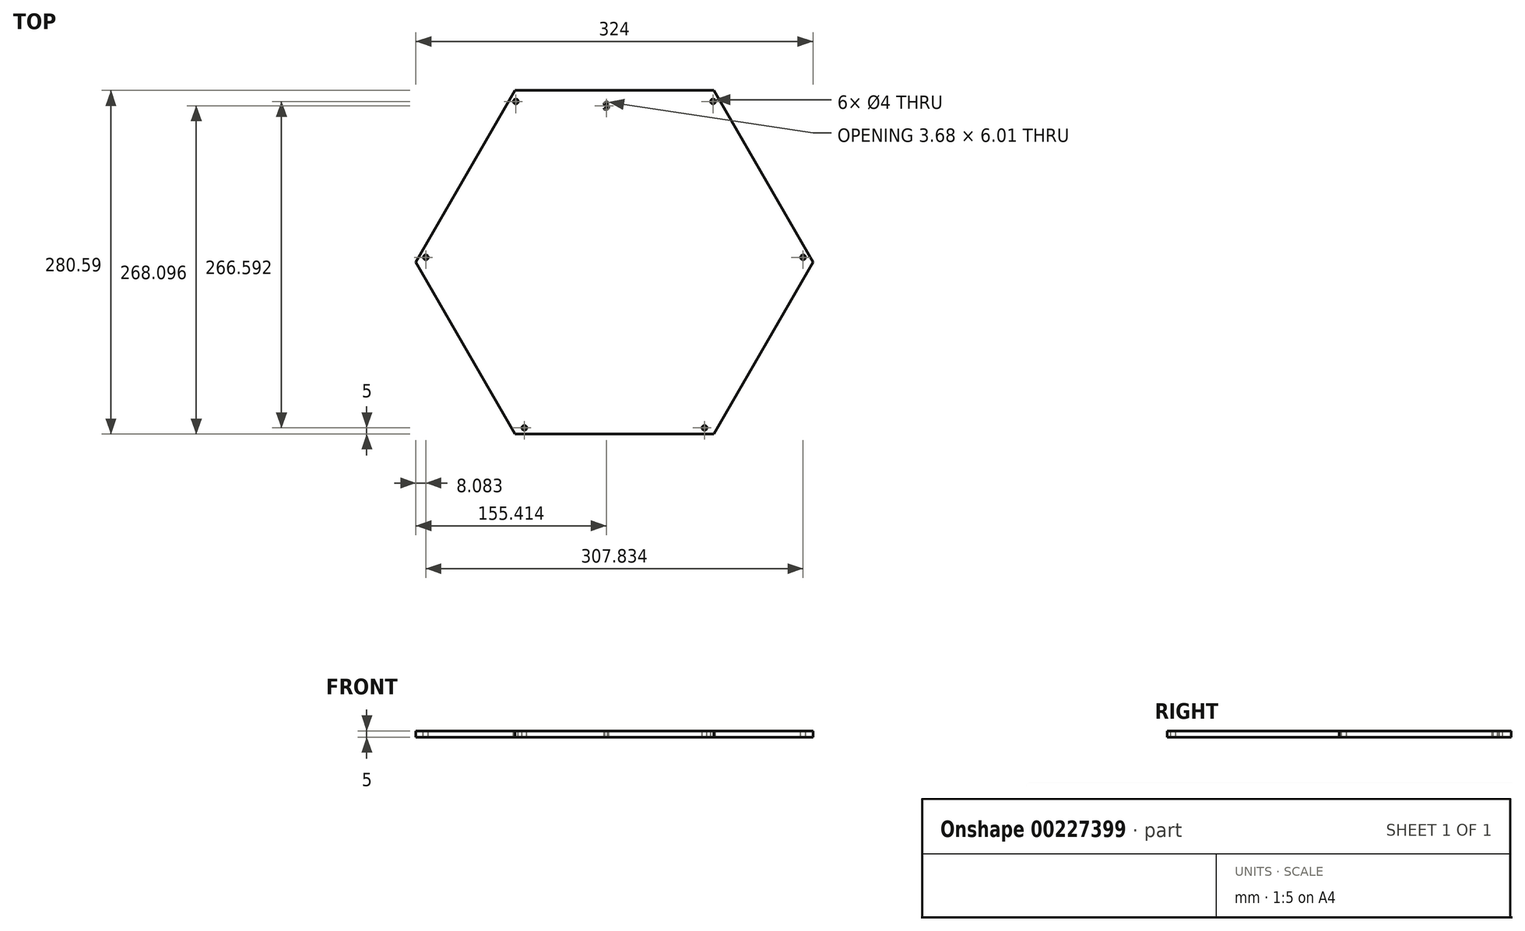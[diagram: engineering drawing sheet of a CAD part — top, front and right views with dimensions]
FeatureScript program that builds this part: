
annotation { "Feature Type Name" : "Feature", "Feature Type Description" : "" }
export const myFeature = defineFeature(function(context is Context, id is Id, definition is map)
    precondition{}
    {
        {
            var Q0;
            Q0=qCreatedBy(makeId("Top.planeOp"),FACE);
            var sketch = newSketch(context, id + "F0", { "sketchPlane" : qUnion([Q0])});
            skLineSegment(sketch, "E0", {"start": v(-81, 0) * mm, "end": v(81, 0) * mm});
            skLineSegment(sketch, "E1", {"start": v(-81, 280.6) * mm, "end": v(-162, 140.3) * mm});
            skCircle(sketch, "E2", {"center": v(0, 140.3) * mm, "radius": 140.3 * mm, "construction": true});
            skLineSegment(sketch, "E3.0", {"start": v(-81, 280.6) * mm, "end": v(81, 280.6) * mm});
            skLineSegment(sketch, "E3.2", {"start": v(162, 140.3) * mm, "end": v(81, 0) * mm});
            skLineSegment(sketch, "E3.4", {"start": v(-81, 0) * mm, "end": v(-162, 140.3) * mm});
            skPoint(sketch, "E3.0.midPoint", {"position": v(0, 280.6) * mm});
            skPoint(sketch, "E4.orphan", {"position": v(0, 420.89) * mm});
            skPoint(sketch, "E5.orphan", {"position": v(-243, 0) * mm});
            skPoint(sketch, "E6.orphan", {"position": v(243, 0) * mm});
            skLineSegment(sketch, "E7", {"start": v(81, 280.6) * mm, "end": v(162, 140.3) * mm});
            skSolve(sketch);
        }
        {
            var Q0;
            Q0 = qSketchRegion(id + "F0", true);
            extrude(context, id + "F1", {"entities" : qUnion([Q0]), "depth" : 5 * mm});
        }
        {
            var Q0;
            Q0=makeQuery(id+"F1.opExtrude","CAP_FACE",FACE,{"disambiguationData":[OSD([sQuery(id+"F0.wireOp",EDGE,"E0"),sQuery(id+"F0.wireOp",EDGE,"E1"),sQuery(id+"F0.wireOp",EDGE,"E3.0"),sQuery(id+"F0.wireOp",EDGE,"E3.2"),sQuery(id+"F0.wireOp",EDGE,"E3.4"),sQuery(id+"F0.wireOp",EDGE,"E7")])],"isStart":false});
            var sketch = newSketch(context, id + "F2", { "sketchPlane" : qUnion([Q0])});
            skLineSegment(sketch, "E8.0", {"start": v(-81, 271.6) * mm, "end": v(81, 271.6) * mm});
            skLineSegment(sketch, "E9.0", {"start": v(-76.67, 278.1) * mm, "end": v(-157.67, 137.8) * mm});
            skPoint(sketch, "E10", {"position": v(-80.42, 271.6) * mm});
            skPoint(sketch, "E11.centerSnap0", {"position": v(0, 271.6) * mm});
            skCircle(sketch, "E12", {"center": v(-80.42, 271.6) * mm, "radius": 2 * mm});
            skLineSegment(sketch, "E13.0", {"start": v(-73.2, 4.5) * mm, "end": v(-154.2, 144.8) * mm});
            skLineSegment(sketch, "E14.0", {"start": v(154.2, 144.8) * mm, "end": v(73.2, 4.5) * mm});
            skLineSegment(sketch, "E15.0", {"start": v(76.67, 278.1) * mm, "end": v(157.67, 137.8) * mm});
            skPoint(sketch, "E16", {"position": v(80.42, 271.6) * mm});
            skCircle(sketch, "E17", {"center": v(80.42, 271.6) * mm, "radius": 2 * mm});
            skLineSegment(sketch, "E18.0", {"start": v(-81, 5) * mm, "end": v(81, 5) * mm});
            skPoint(sketch, "E19", {"position": v(-73.5, 5) * mm});
            skPoint(sketch, "E20", {"position": v(73.5, 5) * mm});
            skPoint(sketch, "E21", {"position": v(153.92, 144.3) * mm});
            skPoint(sketch, "E22", {"position": v(-153.92, 144.3) * mm});
            skCircle(sketch, "E23", {"center": v(-153.92, 144.3) * mm, "radius": 2 * mm});
            skCircle(sketch, "E24", {"center": v(-73.5, 5) * mm, "radius": 2 * mm});
            skCircle(sketch, "E25", {"center": v(73.5, 5) * mm, "radius": 2 * mm});
            skCircle(sketch, "E26", {"center": v(153.92, 144.3) * mm, "radius": 2 * mm});
            skSolve(sketch);
        }
        {
            var Q0;
            {var subQ0=sQuery(id+"F2.wireOp",EDGE,"E9.0");var subQ1=sQuery(id+"F2.wireOp",EDGE,"E8.0");var subQ2=makeQuery(id+"F2.imprint","INTERSECT",VERTEX,{"derivedFrom":[subQ1,subQ0]});Q0=makeQuery(id+"F2.imprint","IMPRINT",FACE,{"disambiguationData":[TD([[makeQuery(id+"F2.imprint","IMPRINT",EDGE,{"disambiguationData":[TD([[subQ2,-1.0]])],"derivedFrom":subQ1}),-1.0]])]});}
            var Q1;
            {var subQ0=sQuery(id+"F2.wireOp",EDGE,"E9.0");var subQ1=sQuery(id+"F2.wireOp",EDGE,"E8.0");var subQ2=makeQuery(id+"F2.imprint","INTERSECT",VERTEX,{"derivedFrom":[subQ1,subQ0]});Q1=makeQuery(id+"F2.imprint","IMPRINT",FACE,{"disambiguationData":[TD([[makeQuery(id+"F2.imprint","IMPRINT",EDGE,{"disambiguationData":[TD([[subQ2,-1.0]])],"derivedFrom":subQ1}),1.0]])]});}
            var Q2;
            {var subQ0=sQuery(id+"F2.wireOp",EDGE,"E9.0");var subQ1=makeQuery(id+"F2.imprint","INTERSECT",VERTEX,{"derivedFrom":[sQuery(id+"F2.wireOp",EDGE,"E8.0"),subQ0]});Q2=makeQuery(id+"F2.imprint","IMPRINT",FACE,{"disambiguationData":[TD([[makeQuery(id+"F2.imprint","IMPRINT",EDGE,{"disambiguationData":[TD([[subQ1,1.0]])],"derivedFrom":subQ0}),-1.0]])]});}
            var Q3;
            {var subQ0=sQuery(id+"F2.wireOp",EDGE,"E15.0");var subQ1=makeQuery(id+"F2.imprint","INTERSECT",VERTEX,{"derivedFrom":[sQuery(id+"F2.wireOp",EDGE,"E8.0"),subQ0]});Q3=makeQuery(id+"F2.imprint","IMPRINT",FACE,{"disambiguationData":[TD([[makeQuery(id+"F2.imprint","IMPRINT",EDGE,{"disambiguationData":[TD([[subQ1,1.0]])],"derivedFrom":subQ0}),1.0]])]});}
            var Q4;
            {var subQ0=sQuery(id+"F2.wireOp",EDGE,"E15.0");var subQ1=sQuery(id+"F2.wireOp",EDGE,"E8.0");var subQ2=makeQuery(id+"F2.imprint","INTERSECT",VERTEX,{"derivedFrom":[subQ1,subQ0]});Q4=makeQuery(id+"F2.imprint","IMPRINT",FACE,{"disambiguationData":[TD([[makeQuery(id+"F2.imprint","IMPRINT",EDGE,{"disambiguationData":[TD([[subQ2,1.0]])],"derivedFrom":subQ1}),1.0]])]});}
            var Q5;
            {var subQ0=sQuery(id+"F2.wireOp",EDGE,"E15.0");var subQ1=sQuery(id+"F2.wireOp",EDGE,"E8.0");var subQ2=makeQuery(id+"F2.imprint","INTERSECT",VERTEX,{"derivedFrom":[subQ1,subQ0]});Q5=makeQuery(id+"F2.imprint","IMPRINT",FACE,{"disambiguationData":[TD([[makeQuery(id+"F2.imprint","IMPRINT",EDGE,{"disambiguationData":[TD([[subQ2,1.0]])],"derivedFrom":subQ1}),-1.0]])]});}
            var Q6;
            {var subQ0=sQuery(id+"F2.wireOp",EDGE,"E15.0");var subQ1=makeQuery(id+"F2.imprint","INTERSECT",VERTEX,{"derivedFrom":[sQuery(id+"F2.wireOp",EDGE,"E14.0"),subQ0]});Q6=makeQuery(id+"F2.imprint","IMPRINT",FACE,{"disambiguationData":[TD([[makeQuery(id+"F2.imprint","IMPRINT",EDGE,{"disambiguationData":[TD([[subQ1,1.0]])],"derivedFrom":subQ0}),1.0]])]});}
            var Q7;
            {var subQ0=sQuery(id+"F2.wireOp",EDGE,"E15.0");var subQ1=sQuery(id+"F2.wireOp",EDGE,"E14.0");var subQ2=makeQuery(id+"F2.imprint","INTERSECT",VERTEX,{"derivedFrom":[subQ1,subQ0]});Q7=makeQuery(id+"F2.imprint","IMPRINT",FACE,{"disambiguationData":[TD([[makeQuery(id+"F2.imprint","IMPRINT",EDGE,{"disambiguationData":[TD([[subQ2,-1.0]])],"derivedFrom":subQ1}),1.0]])]});}
            var Q8;
            {var subQ0=sQuery(id+"F2.wireOp",EDGE,"E15.0");var subQ1=sQuery(id+"F2.wireOp",EDGE,"E14.0");var subQ2=makeQuery(id+"F2.imprint","INTERSECT",VERTEX,{"derivedFrom":[subQ1,subQ0]});Q8=makeQuery(id+"F2.imprint","IMPRINT",FACE,{"disambiguationData":[TD([[makeQuery(id+"F2.imprint","IMPRINT",EDGE,{"disambiguationData":[TD([[subQ2,-1.0]])],"derivedFrom":subQ1}),-1.0]])]});}
            var Q9;
            {var subQ0=sQuery(id+"F2.wireOp",EDGE,"E18.0");var subQ1=sQuery(id+"F2.wireOp",EDGE,"E14.0");var subQ2=makeQuery(id+"F2.imprint","INTERSECT",VERTEX,{"derivedFrom":[subQ1,subQ0]});Q9=makeQuery(id+"F2.imprint","IMPRINT",FACE,{"disambiguationData":[TD([[makeQuery(id+"F2.imprint","IMPRINT",EDGE,{"disambiguationData":[TD([[subQ2,1.0]])],"derivedFrom":subQ1}),-1.0]])]});}
            var Q10;
            {var subQ0=sQuery(id+"F2.wireOp",EDGE,"E18.0");var subQ1=sQuery(id+"F2.wireOp",EDGE,"E14.0");var subQ2=makeQuery(id+"F2.imprint","INTERSECT",VERTEX,{"derivedFrom":[subQ1,subQ0]});Q10=makeQuery(id+"F2.imprint","IMPRINT",FACE,{"disambiguationData":[TD([[makeQuery(id+"F2.imprint","IMPRINT",EDGE,{"disambiguationData":[TD([[subQ2,1.0]])],"derivedFrom":subQ1}),1.0]])]});}
            var Q11;
            {var subQ0=sQuery(id+"F2.wireOp",EDGE,"E18.0");var subQ1=makeQuery(id+"F2.imprint","INTERSECT",VERTEX,{"derivedFrom":[sQuery(id+"F2.wireOp",EDGE,"E14.0"),subQ0]});Q11=makeQuery(id+"F2.imprint","IMPRINT",FACE,{"disambiguationData":[TD([[makeQuery(id+"F2.imprint","IMPRINT",EDGE,{"disambiguationData":[TD([[subQ1,1.0]])],"derivedFrom":subQ0}),-1.0]])]});}
            var Q12;
            {var subQ0=sQuery(id+"F2.wireOp",EDGE,"E18.0");var subQ1=sQuery(id+"F2.wireOp",EDGE,"E13.0");var subQ2=makeQuery(id+"F2.imprint","INTERSECT",VERTEX,{"derivedFrom":[subQ1,subQ0]});Q12=makeQuery(id+"F2.imprint","IMPRINT",FACE,{"disambiguationData":[TD([[makeQuery(id+"F2.imprint","IMPRINT",EDGE,{"disambiguationData":[TD([[subQ2,-1.0]])],"derivedFrom":subQ1}),-1.0]])]});}
            var Q13;
            {var subQ0=sQuery(id+"F2.wireOp",EDGE,"E18.0");var subQ1=sQuery(id+"F2.wireOp",EDGE,"E13.0");var subQ2=makeQuery(id+"F2.imprint","INTERSECT",VERTEX,{"derivedFrom":[subQ1,subQ0]});Q13=makeQuery(id+"F2.imprint","IMPRINT",FACE,{"disambiguationData":[TD([[makeQuery(id+"F2.imprint","IMPRINT",EDGE,{"disambiguationData":[TD([[subQ2,-1.0]])],"derivedFrom":subQ1}),1.0]])]});}
            var Q14;
            {var subQ0=sQuery(id+"F2.wireOp",EDGE,"E18.0");var subQ1=makeQuery(id+"F2.imprint","INTERSECT",VERTEX,{"derivedFrom":[sQuery(id+"F2.wireOp",EDGE,"E13.0"),subQ0]});Q14=makeQuery(id+"F2.imprint","IMPRINT",FACE,{"disambiguationData":[TD([[makeQuery(id+"F2.imprint","IMPRINT",EDGE,{"disambiguationData":[TD([[subQ1,1.0]])],"derivedFrom":subQ0}),-1.0]])]});}
            var Q15;
            {var subQ0=sQuery(id+"F2.wireOp",EDGE,"E13.0");var subQ1=sQuery(id+"F2.wireOp",EDGE,"E9.0");var subQ2=makeQuery(id+"F2.imprint","INTERSECT",VERTEX,{"derivedFrom":[subQ1,subQ0]});Q15=makeQuery(id+"F2.imprint","IMPRINT",FACE,{"disambiguationData":[TD([[makeQuery(id+"F2.imprint","IMPRINT",EDGE,{"disambiguationData":[TD([[subQ2,1.0]])],"derivedFrom":subQ1}),1.0]])]});}
            var Q16;
            {var subQ0=sQuery(id+"F2.wireOp",EDGE,"E9.0");var subQ1=makeQuery(id+"F2.imprint","INTERSECT",VERTEX,{"derivedFrom":[subQ0,sQuery(id+"F2.wireOp",EDGE,"E13.0")]});Q16=makeQuery(id+"F2.imprint","IMPRINT",FACE,{"disambiguationData":[TD([[makeQuery(id+"F2.imprint","IMPRINT",EDGE,{"disambiguationData":[TD([[subQ1,1.0]])],"derivedFrom":subQ0}),-1.0]])]});}
            var Q17;
            {var subQ0=sQuery(id+"F2.wireOp",EDGE,"E13.0");var subQ1=sQuery(id+"F2.wireOp",EDGE,"E9.0");var subQ2=makeQuery(id+"F2.imprint","INTERSECT",VERTEX,{"derivedFrom":[subQ1,subQ0]});Q17=makeQuery(id+"F2.imprint","IMPRINT",FACE,{"disambiguationData":[TD([[makeQuery(id+"F2.imprint","IMPRINT",EDGE,{"disambiguationData":[TD([[subQ2,-1.0]])],"derivedFrom":subQ1}),1.0]])]});}
            extrude(context, id + "F3", {"entities" : qUnion([Q0, Q1, Q2, Q3, Q4, Q5, Q6, Q7, Q8, Q9, Q10, Q11, Q12, Q13, Q14, Q15, Q16, Q17]), "operationType" : NewBodyOperationType.REMOVE, "oppositeDirection" : true, "depth" : 25 * mm});
        }
        {
            var Q0;
            Q0=makeQuery(id+"F1.opExtrude","CAP_FACE",FACE,{"disambiguationData":[OSD([sQuery(id+"F0.wireOp",EDGE,"E0"),sQuery(id+"F0.wireOp",EDGE,"E1"),sQuery(id+"F0.wireOp",EDGE,"E3.0"),sQuery(id+"F0.wireOp",EDGE,"E3.2"),sQuery(id+"F0.wireOp",EDGE,"E3.4"),sQuery(id+"F0.wireOp",EDGE,"E7")])],"isStart":false});
            var sketch = newSketch(context, id + "F4", { "sketchPlane" : qUnion([Q0])});
            skText(sketch, "E27", { "text": "S", "fontName": "OpenSans-Regular.ttf"});
            const initialGuessF4  = {"E27": [-0.00885, 0.26517, 1, 0, 0.0059]};
            skSetInitialGuess(sketch, initialGuessF4);
            skSolve(sketch);
        }
        {
            var Q0;
            Q0=makeQuery(id+"F4.imprint","IMPRINT",FACE,{"disambiguationData":[TD([[makeQuery(id+"F4.imprint","IMPRINT",EDGE,{"derivedFrom":sQuery(id+"F4.wireOp",EDGE,"E27.sketch_text.stroke-0")}),-1.0]])]});
            extrude(context, id + "F5", {"entities" : qUnion([Q0]), "operationType" : NewBodyOperationType.REMOVE, "oppositeDirection" : true, "depth" : 25 * mm});
        }
    });
